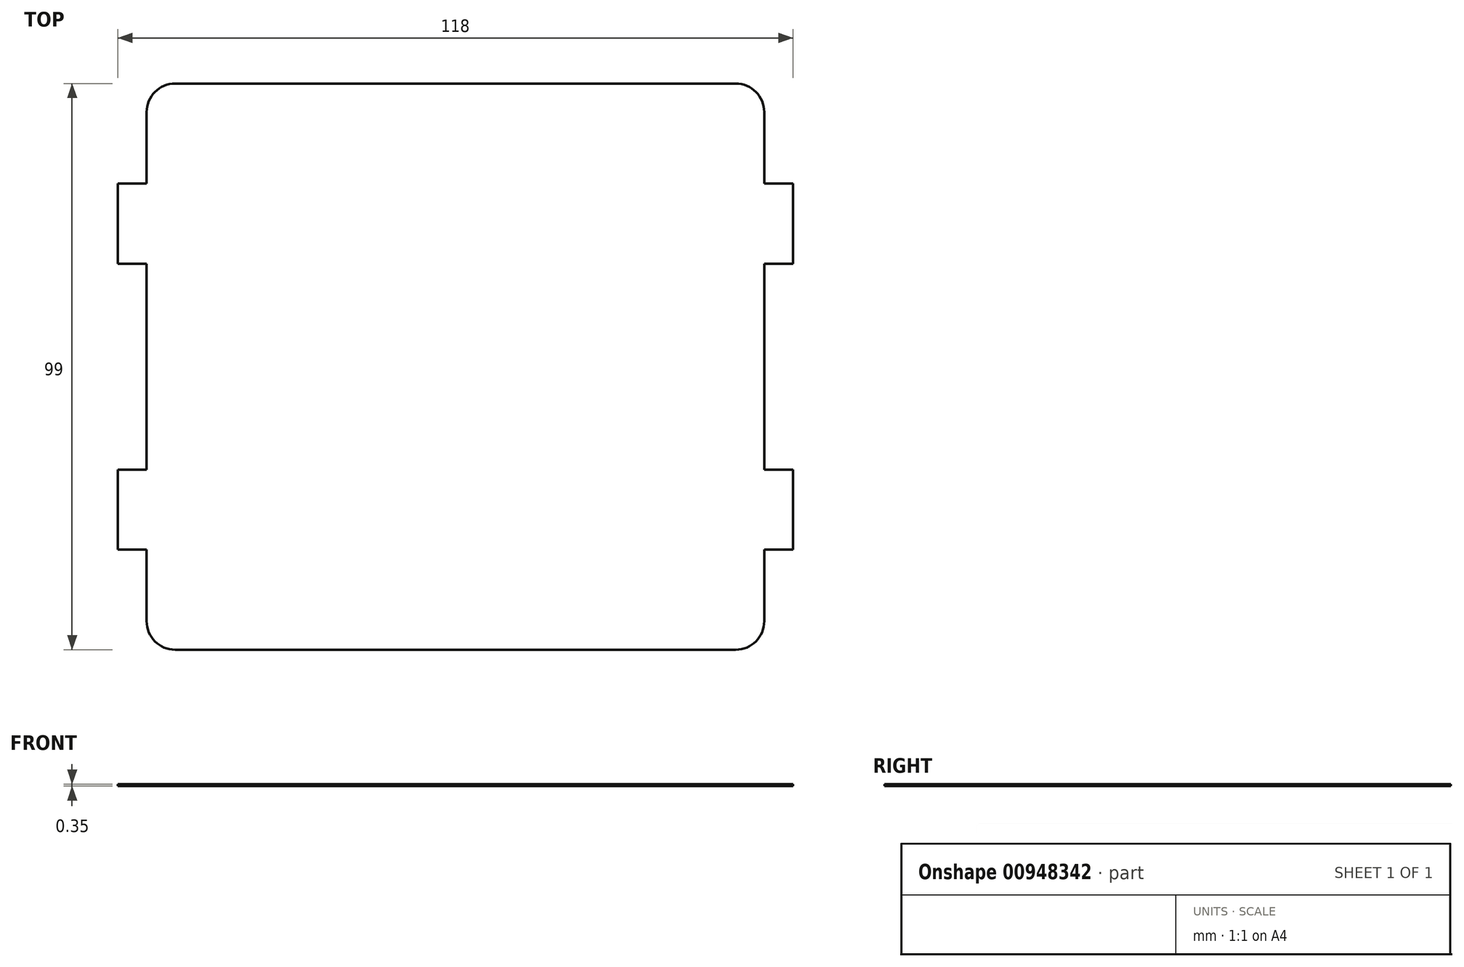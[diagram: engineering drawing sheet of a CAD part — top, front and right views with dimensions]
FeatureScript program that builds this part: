
annotation { "Feature Type Name" : "Feature", "Feature Type Description" : "" }
export const myFeature = defineFeature(function(context is Context, id is Id, definition is map)
    precondition{}
    {
        {
            var Q0;
            Q0=qCreatedBy(makeId("Top.planeOp"),FACE);
            var sketch = newSketch(context, id + "F0", { "sketchPlane" : qUnion([Q0])});
            skLineSegment(sketch, "E0.bottom", {"start": v(49, 49.5) * mm, "end": v(-49, 49.5) * mm});
            skLineSegment(sketch, "E0.top", {"start": v(49, -49.5) * mm, "end": v(-49, -49.5) * mm});
            skLineSegment(sketch, "E0.left", {"start": v(54, 44.5) * mm, "end": v(54, -44.5) * mm});
            skLineSegment(sketch, "E0.right", {"start": v(-54, 44.5) * mm, "end": v(-54, -44.5) * mm});
            skPoint(sketch, "E0.middle", {"position": v(0, 0) * mm});
            skLineSegment(sketch, "E1.bottom", {"start": v(-59, 18) * mm, "end": v(59, 18) * mm});
            skLineSegment(sketch, "E1.top", {"start": v(-59, 32) * mm, "end": v(59, 32) * mm});
            skLineSegment(sketch, "E1.left", {"start": v(-59, 18) * mm, "end": v(-59, 32) * mm});
            skLineSegment(sketch, "E1.right", {"start": v(59, 18) * mm, "end": v(59, 32) * mm});
            skPoint(sketch, "E1.middle", {"position": v(0, 25) * mm});
            skLineSegment(sketch, "E2", {"start": v(0, 0) * mm, "end": v(0, 25) * mm});
            skLineSegment(sketch, "E3.MirrorCS", {"start": v(-59, -18) * mm, "end": v(59, -18) * mm});
            skLineSegment(sketch, "E4.MirrorCS", {"start": v(-59, -18) * mm, "end": v(-59, -32) * mm});
            skLineSegment(sketch, "E5.MirrorCS", {"start": v(-59, -32) * mm, "end": v(59, -32) * mm});
            skLineSegment(sketch, "E6.MirrorCS", {"start": v(59, -18) * mm, "end": v(59, -32) * mm});
            skPoint(sketch, "E7.visualSharp", {"position": v(-54, 49.5) * mm});
            skArc(sketch, "E7.filletArc", {"start": v(-49, 49.5) * mm, "mid": v(-52.54, 48.04) * mm, "end": v(-54, 44.5) * mm});
            skPoint(sketch, "E8.visualSharp", {"position": v(54, 49.5) * mm});
            skArc(sketch, "E8.filletArc", {"start": v(54, 44.5) * mm, "mid": v(52.54, 48.04) * mm, "end": v(49, 49.5) * mm});
            skPoint(sketch, "E9.visualSharp", {"position": v(54, -49.5) * mm});
            skArc(sketch, "E9.filletArc", {"start": v(49, -49.5) * mm, "mid": v(52.54, -48.04) * mm, "end": v(54, -44.5) * mm});
            skPoint(sketch, "E10.visualSharp", {"position": v(-54, -49.5) * mm});
            skArc(sketch, "E10.filletArc", {"start": v(-54, -44.5) * mm, "mid": v(-52.54, -48.04) * mm, "end": v(-49, -49.5) * mm});
            skSolve(sketch);
        }
        {
            var Q0;
            {var subQ0=sQuery(id+"F0.wireOp",EDGE,"E1.bottom");var subQ1=makeQuery(id+"F0.imprint","IMPRINT",VERTEX,{"derivedFrom":subQ0});Q0=makeQuery(id+"F0.imprint","IMPRINT",FACE,{"disambiguationData":[TD([[makeQuery(id+"F0.imprint","IMPRINT",EDGE,{"disambiguationData":[TD([[subQ1,1.0]])],"derivedFrom":subQ0}),1.0]])]});}
            var Q1;
            Q1=makeQuery(id+"F0.imprint","IMPRINT",FACE,{"disambiguationData":[TD([[makeQuery(id+"F0.imprint","IMPRINT",EDGE,{"derivedFrom":sQuery(id+"F0.wireOp",EDGE,"E0.bottom")}),1.0]])]});
            var Q2;
            {var subQ5=sQuery(id+"F0.wireOp",EDGE,"E1.left");Q2=makeQuery(id+"F0.imprint","IMPRINT",FACE,{"disambiguationData":[TD([[makeQuery(id+"F0.imprint","IMPRINT",EDGE,{"derivedFrom":subQ5}),-1.0]])]});}
            var Q3;
            {var subQ0=sQuery(id+"F0.wireOp",EDGE,"E1.bottom");var subQ1=makeQuery(id+"F0.imprint","IMPRINT",VERTEX,{"derivedFrom":subQ0});Q3=makeQuery(id+"F0.imprint","IMPRINT",FACE,{"disambiguationData":[TD([[makeQuery(id+"F0.imprint","IMPRINT",EDGE,{"disambiguationData":[TD([[subQ1,1.0]])],"derivedFrom":subQ0}),-1.0]])]});}
            var Q4;
            {var subQ0=sQuery(id+"F0.wireOp",EDGE,"E3.MirrorCS");var subQ1=sQuery(id+"F0.wireOp",EDGE,"E0.left");var subQ2=makeQuery(id+"F0.imprint","INTERSECT",VERTEX,{"derivedFrom":[subQ1,subQ0]});Q4=makeQuery(id+"F0.imprint","IMPRINT",FACE,{"disambiguationData":[TD([[makeQuery(id+"F0.imprint","IMPRINT",EDGE,{"disambiguationData":[TD([[subQ2,-1.0]])],"derivedFrom":subQ1}),-1.0]])]});}
            var Q5;
            {var subQ5=sQuery(id+"F0.wireOp",EDGE,"E4.MirrorCS");Q5=makeQuery(id+"F0.imprint","IMPRINT",FACE,{"disambiguationData":[TD([[makeQuery(id+"F0.imprint","IMPRINT",EDGE,{"derivedFrom":subQ5}),1.0]])]});}
            var Q6;
            Q6=makeQuery(id+"F0.imprint","IMPRINT",FACE,{"disambiguationData":[TD([[makeQuery(id+"F0.imprint","IMPRINT",EDGE,{"derivedFrom":sQuery(id+"F0.wireOp",EDGE,"E0.top")}),-1.0]])]});
            var Q7;
            {var subQ5=sQuery(id+"F0.wireOp",EDGE,"E6.MirrorCS");Q7=makeQuery(id+"F0.imprint","IMPRINT",FACE,{"disambiguationData":[TD([[makeQuery(id+"F0.imprint","IMPRINT",EDGE,{"derivedFrom":subQ5}),-1.0]])]});}
            var Q8;
            {var subQ5=sQuery(id+"F0.wireOp",EDGE,"E1.right");Q8=makeQuery(id+"F0.imprint","IMPRINT",FACE,{"disambiguationData":[TD([[makeQuery(id+"F0.imprint","IMPRINT",EDGE,{"derivedFrom":subQ5}),1.0]])]});}
            extrude(context, id + "F1", {"entities" : qUnion([Q0, Q1, Q2, Q3, Q4, Q5, Q6, Q7, Q8]), "depth" : 0.35 * mm, "offsetDistance" : 25 * mm});
        }
    });
